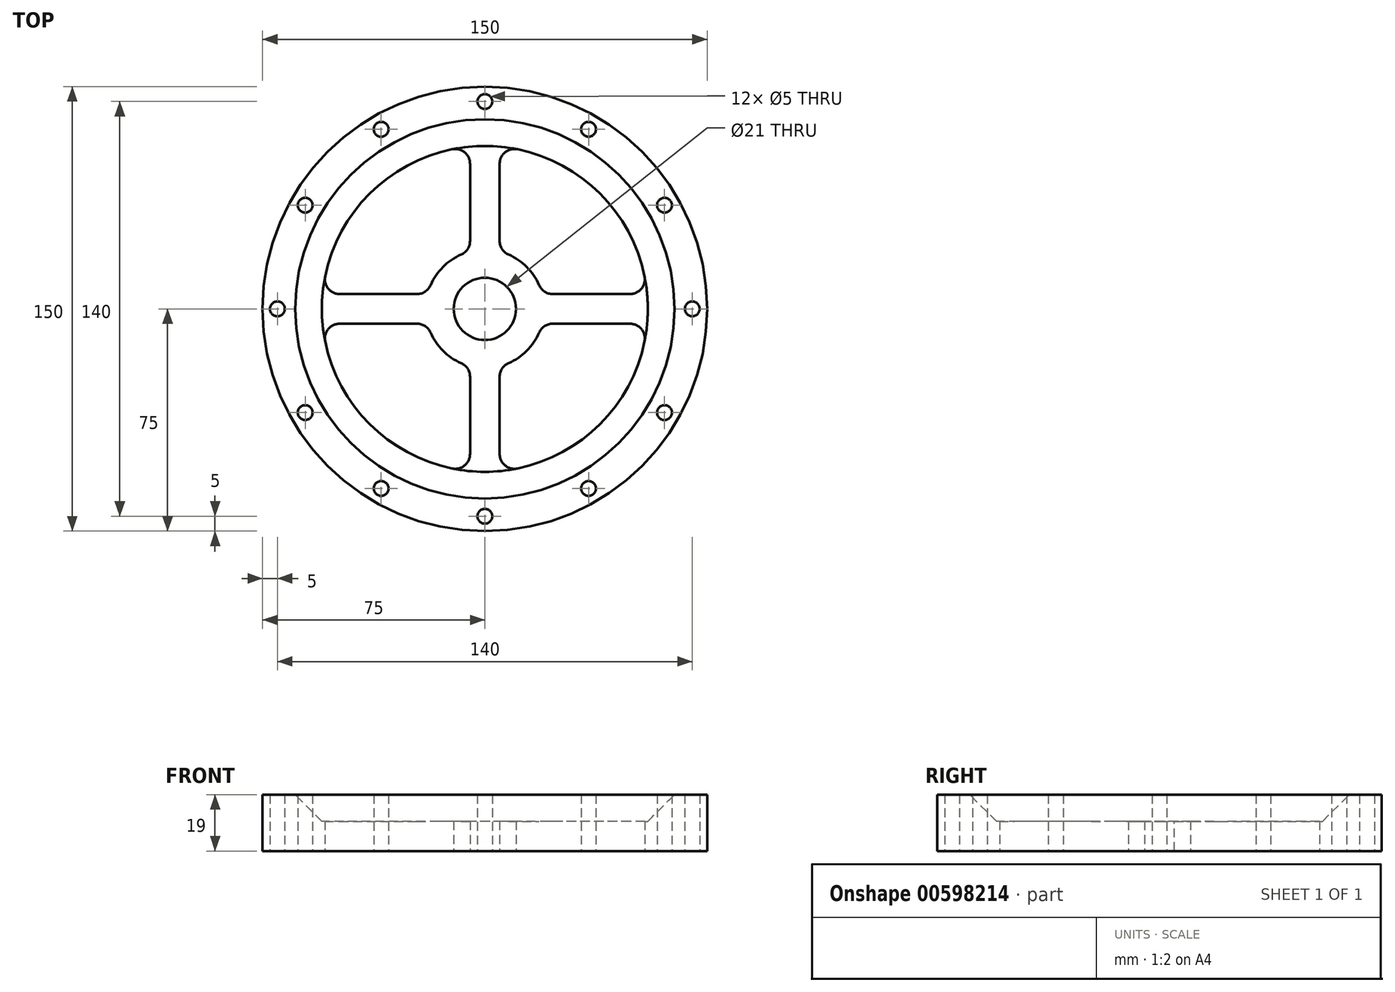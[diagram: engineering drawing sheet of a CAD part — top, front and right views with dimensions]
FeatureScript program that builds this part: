
annotation { "Feature Type Name" : "Feature", "Feature Type Description" : "" }
export const myFeature = defineFeature(function(context is Context, id is Id, definition is map)
    precondition{}
    {
        {
            var Q0;
            Q0=qCreatedBy(makeId("Top.planeOp"),FACE);
            var sketch = newSketch(context, id + "F0", { "sketchPlane" : qUnion([Q0])});
            skCircle(sketch, "E0", {"center": v(0, 0) * mm, "radius": 10.5 * mm});
            skCircle(sketch, "E1", {"center": v(0, 0) * mm, "radius": 75 * mm});
            skArc(sketch, "E2", {"start": v(54.77, 5) * mm, "mid": v(38.9, 38.9) * mm, "end": v(5, 54.77) * mm});
            skArc(sketch, "E3", {"start": v(-5, 19.36) * mm, "mid": v(-14.14, 14.14) * mm, "end": v(-19.36, 5) * mm});
            skLineSegment(sketch, "E4", {"start": v(54.77, -5) * mm, "end": v(19.36, -5) * mm});
            skLineSegment(sketch, "E5", {"start": v(5, 54.77) * mm, "end": v(5, 19.36) * mm});
            skLineSegment(sketch, "E6.trimOffspring", {"start": v(5, -19.36) * mm, "end": v(5, -54.77) * mm});
            skLineSegment(sketch, "E7.MirrorCS", {"start": v(54.77, 5) * mm, "end": v(19.36, 5) * mm});
            skLineSegment(sketch, "E8.MirrorCS", {"start": v(-5, 54.77) * mm, "end": v(-5, 19.36) * mm});
            skLineSegment(sketch, "E9.MirrorCS", {"start": v(-54.77, 5) * mm, "end": v(-19.36, 5) * mm});
            skLineSegment(sketch, "E10.MirrorCS", {"start": v(-54.77, -5) * mm, "end": v(-19.36, -5) * mm});
            skLineSegment(sketch, "E11.MirrorCS", {"start": v(-5, -19.36) * mm, "end": v(-5, -54.77) * mm});
            skArc(sketch, "E12.trimOffspring", {"start": v(-5, 54.77) * mm, "mid": v(-38.9, 38.9) * mm, "end": v(-54.77, 5) * mm});
            skArc(sketch, "E13.trimOffspring", {"start": v(19.36, 5) * mm, "mid": v(14.14, 14.14) * mm, "end": v(5, 19.36) * mm});
            skArc(sketch, "E14.trimOffspring", {"start": v(-19.36, -5) * mm, "mid": v(-14.14, -14.14) * mm, "end": v(-5, -19.36) * mm});
            skArc(sketch, "E15.trimOffspring", {"start": v(-54.77, -5) * mm, "mid": v(-38.9, -38.9) * mm, "end": v(-5, -54.77) * mm});
            skArc(sketch, "E16.trimOffspring", {"start": v(5, -19.36) * mm, "mid": v(14.14, -14.14) * mm, "end": v(19.36, -5) * mm});
            skArc(sketch, "E17.trimOffspring", {"start": v(5, -54.77) * mm, "mid": v(38.9, -38.9) * mm, "end": v(54.77, -5) * mm});
            skCircle(sketch, "E18", {"center": v(70, 0) * mm, "radius": 2.5 * mm});
            skCircle(sketch, "E19.1.0", {"center": v(60.62, 35) * mm, "radius": 2.5 * mm});
            skCircle(sketch, "E19.2.0", {"center": v(35, 60.62) * mm, "radius": 2.5 * mm});
            skCircle(sketch, "E19.3.0", {"center": v(0, 70) * mm, "radius": 2.5 * mm});
            skCircle(sketch, "E19.4.0", {"center": v(-35, 60.62) * mm, "radius": 2.5 * mm});
            skCircle(sketch, "E19.5.0", {"center": v(-60.62, 35) * mm, "radius": 2.5 * mm});
            skCircle(sketch, "E19.6.0", {"center": v(-70, 0) * mm, "radius": 2.5 * mm});
            skCircle(sketch, "E19.7.0", {"center": v(-60.62, -35) * mm, "radius": 2.5 * mm});
            skCircle(sketch, "E19.8.0", {"center": v(-35, -60.62) * mm, "radius": 2.5 * mm});
            skCircle(sketch, "E19.9.0", {"center": v(0, -70) * mm, "radius": 2.5 * mm});
            skCircle(sketch, "E19.10.0", {"center": v(35, -60.62) * mm, "radius": 2.5 * mm});
            skCircle(sketch, "E19.11.0", {"center": v(60.62, -35) * mm, "radius": 2.5 * mm});
            skSolve(sketch);
        }
        {
            var Q0;
            Q0=makeQuery(id+"F0.imprint","IMPRINT",FACE,{"disambiguationData":[TD([[makeQuery(id+"F0.imprint","IMPRINT",EDGE,{"derivedFrom":sQuery(id+"F0.wireOp",EDGE,"E0")}),-1.0]])]});
            extrude(context, id + "F1", {"entities" : qUnion([Q0]), "depth" : 10 * mm, "offsetDistance" : 25 * mm});
        }
        {
            var Q0;
            Q0=makeQuery(id+"F1.opExtrude","SWEPT_EDGE",EDGE,{"disambiguationData":[OSD([sQuery(id+"F0.wireOp",EDGE,"E6.trimOffspring"),sQuery(id+"F0.wireOp",EDGE,"E17.trimOffspring")])]});
            var Q1;
            Q1=makeQuery(id+"F1.opExtrude","SWEPT_EDGE",EDGE,{"disambiguationData":[OSD([sQuery(id+"F0.wireOp",EDGE,"E6.trimOffspring"),sQuery(id+"F0.wireOp",EDGE,"E16.trimOffspring")])]});
            var Q2;
            Q2=makeQuery(id+"F1.opExtrude","SWEPT_EDGE",EDGE,{"disambiguationData":[OSD([sQuery(id+"F0.wireOp",EDGE,"E4"),sQuery(id+"F0.wireOp",EDGE,"E16.trimOffspring")])]});
            var Q3;
            Q3=makeQuery(id+"F1.opExtrude","SWEPT_EDGE",EDGE,{"disambiguationData":[OSD([sQuery(id+"F0.wireOp",EDGE,"E7.MirrorCS"),sQuery(id+"F0.wireOp",EDGE,"E13.trimOffspring")])]});
            var Q4;
            Q4=makeQuery(id+"F1.opExtrude","SWEPT_EDGE",EDGE,{"disambiguationData":[OSD([sQuery(id+"F0.wireOp",EDGE,"E5"),sQuery(id+"F0.wireOp",EDGE,"E13.trimOffspring")])]});
            var Q5;
            Q5=makeQuery(id+"F1.opExtrude","SWEPT_EDGE",EDGE,{"disambiguationData":[OSD([sQuery(id+"F0.wireOp",EDGE,"E3"),sQuery(id+"F0.wireOp",EDGE,"E8.MirrorCS")])]});
            var Q6;
            Q6=makeQuery(id+"F1.opExtrude","SWEPT_EDGE",EDGE,{"disambiguationData":[OSD([sQuery(id+"F0.wireOp",EDGE,"E3"),sQuery(id+"F0.wireOp",EDGE,"E9.MirrorCS")])]});
            var Q7;
            Q7=makeQuery(id+"F1.opExtrude","SWEPT_EDGE",EDGE,{"disambiguationData":[OSD([sQuery(id+"F0.wireOp",EDGE,"E11.MirrorCS"),sQuery(id+"F0.wireOp",EDGE,"E14.trimOffspring")])]});
            var Q8;
            Q8=makeQuery(id+"F1.opExtrude","SWEPT_EDGE",EDGE,{"disambiguationData":[OSD([sQuery(id+"F0.wireOp",EDGE,"E10.MirrorCS"),sQuery(id+"F0.wireOp",EDGE,"E14.trimOffspring")])]});
            var Q9;
            Q9=makeQuery(id+"F1.opExtrude","SWEPT_EDGE",EDGE,{"disambiguationData":[OSD([sQuery(id+"F0.wireOp",EDGE,"E2"),sQuery(id+"F0.wireOp",EDGE,"E7.MirrorCS")])]});
            var Q10;
            Q10=makeQuery(id+"F1.opExtrude","SWEPT_EDGE",EDGE,{"disambiguationData":[OSD([sQuery(id+"F0.wireOp",EDGE,"E4"),sQuery(id+"F0.wireOp",EDGE,"E17.trimOffspring")])]});
            var Q11;
            Q11=makeQuery(id+"F1.opExtrude","SWEPT_EDGE",EDGE,{"disambiguationData":[OSD([sQuery(id+"F0.wireOp",EDGE,"E2"),sQuery(id+"F0.wireOp",EDGE,"E5")])]});
            var Q12;
            Q12=makeQuery(id+"F1.opExtrude","SWEPT_EDGE",EDGE,{"disambiguationData":[OSD([sQuery(id+"F0.wireOp",EDGE,"E10.MirrorCS"),sQuery(id+"F0.wireOp",EDGE,"E15.trimOffspring")])]});
            var Q13;
            Q13=makeQuery(id+"F1.opExtrude","SWEPT_EDGE",EDGE,{"disambiguationData":[OSD([sQuery(id+"F0.wireOp",EDGE,"E8.MirrorCS"),sQuery(id+"F0.wireOp",EDGE,"E12.trimOffspring")])]});
            var Q14;
            Q14=makeQuery(id+"F1.opExtrude","SWEPT_EDGE",EDGE,{"disambiguationData":[OSD([sQuery(id+"F0.wireOp",EDGE,"E11.MirrorCS"),sQuery(id+"F0.wireOp",EDGE,"E15.trimOffspring")])]});
            var Q15;
            Q15=makeQuery(id+"F1.opExtrude","SWEPT_EDGE",EDGE,{"disambiguationData":[OSD([sQuery(id+"F0.wireOp",EDGE,"E9.MirrorCS"),sQuery(id+"F0.wireOp",EDGE,"E12.trimOffspring")])]});
            fillet(context, id + "F2", {"entities" : qUnion([Q0, Q1, Q2, Q3, Q4, Q5, Q6, Q7, Q8, Q9, Q10, Q11, Q12, Q13, Q14, Q15]), "radius" : 5 * mm, "tangentPropagation" : true, "allowEdgeOverflow" : false});
        }
        {
            var Q0;
            Q0=makeQuery(id+"F1.opExtrude","CAP_FACE",FACE,{"disambiguationData":[OSD([sQuery(id+"F0.wireOp",EDGE,"E0"),sQuery(id+"F0.wireOp",EDGE,"E1"),sQuery(id+"F0.wireOp",EDGE,"E2"),sQuery(id+"F0.wireOp",EDGE,"E3"),sQuery(id+"F0.wireOp",EDGE,"E4"),sQuery(id+"F0.wireOp",EDGE,"E5"),sQuery(id+"F0.wireOp",EDGE,"E6.trimOffspring"),sQuery(id+"F0.wireOp",EDGE,"E7.MirrorCS"),sQuery(id+"F0.wireOp",EDGE,"E8.MirrorCS"),sQuery(id+"F0.wireOp",EDGE,"E9.MirrorCS"),sQuery(id+"F0.wireOp",EDGE,"E10.MirrorCS"),sQuery(id+"F0.wireOp",EDGE,"E11.MirrorCS"),sQuery(id+"F0.wireOp",EDGE,"E12.trimOffspring"),sQuery(id+"F0.wireOp",EDGE,"E13.trimOffspring"),sQuery(id+"F0.wireOp",EDGE,"E14.trimOffspring"),sQuery(id+"F0.wireOp",EDGE,"E15.trimOffspring"),sQuery(id+"F0.wireOp",EDGE,"E16.trimOffspring"),sQuery(id+"F0.wireOp",EDGE,"E17.trimOffspring"),sQuery(id+"F0.wireOp",EDGE,"E18"),sQuery(id+"F0.wireOp",EDGE,"E19.1.0"),sQuery(id+"F0.wireOp",EDGE,"E19.2.0"),sQuery(id+"F0.wireOp",EDGE,"E19.3.0"),sQuery(id+"F0.wireOp",EDGE,"E19.4.0"),sQuery(id+"F0.wireOp",EDGE,"E19.5.0"),sQuery(id+"F0.wireOp",EDGE,"E19.6.0"),sQuery(id+"F0.wireOp",EDGE,"E19.7.0"),sQuery(id+"F0.wireOp",EDGE,"E19.8.0"),sQuery(id+"F0.wireOp",EDGE,"E19.9.0"),sQuery(id+"F0.wireOp",EDGE,"E19.10.0"),sQuery(id+"F0.wireOp",EDGE,"E19.11.0")])],"isStart":false});
            var sketch = newSketch(context, id + "F3", { "sketchPlane" : qUnion([Q0])});
            skCircle(sketch, "E20", {"center": v(0, 0) * mm, "radius": 75 * mm});
            skCircle(sketch, "E21", {"center": v(0, 0) * mm, "radius": 55 * mm});
            skCircle(sketch, "E22", {"center": v(-70, 0) * mm, "radius": 2.5 * mm});
            skCircle(sketch, "E23.1.0", {"center": v(-60.62, -35) * mm, "radius": 2.5 * mm});
            skCircle(sketch, "E23.2.0", {"center": v(-35, -60.62) * mm, "radius": 2.5 * mm});
            skCircle(sketch, "E23.3.0", {"center": v(0, -70) * mm, "radius": 2.5 * mm});
            skCircle(sketch, "E23.4.0", {"center": v(35, -60.62) * mm, "radius": 2.5 * mm});
            skCircle(sketch, "E23.5.0", {"center": v(60.62, -35) * mm, "radius": 2.5 * mm});
            skCircle(sketch, "E23.6.0", {"center": v(70, 0) * mm, "radius": 2.5 * mm});
            skCircle(sketch, "E23.7.0", {"center": v(60.62, 35) * mm, "radius": 2.5 * mm});
            skCircle(sketch, "E23.8.0", {"center": v(35, 60.62) * mm, "radius": 2.5 * mm});
            skCircle(sketch, "E23.9.0", {"center": v(0, 70) * mm, "radius": 2.5 * mm});
            skCircle(sketch, "E23.10.0", {"center": v(-35, 60.62) * mm, "radius": 2.5 * mm});
            skCircle(sketch, "E23.11.0", {"center": v(-60.62, 35) * mm, "radius": 2.5 * mm});
            skSolve(sketch);
        }
        {
            var Q0;
            Q0=makeQuery(id+"F3.imprint","IMPRINT",FACE,{"disambiguationData":[TD([[makeQuery(id+"F3.imprint","IMPRINT",EDGE,{"derivedFrom":sQuery(id+"F3.wireOp",EDGE,"E20")}),1.0]])]});
            extrude(context, id + "F4", {"entities" : qUnion([Q0]), "operationType" : NewBodyOperationType.ADD, "depth" : 9 * mm, "offsetDistance" : 25 * mm});
        }
        {
            var Q0;
            Q0=makeQuery(id+"F4.opExtrude","CAP_EDGE",EDGE,{"disambiguationData":[OSD([sQuery(id+"F3.wireOp",EDGE,"E21")])],"isStart":false});
            chamfer(context, id + "F5", {"entities" : qUnion([Q0]), "width" : 9 * mm, "tangentPropagation" : true});
        }
    });
